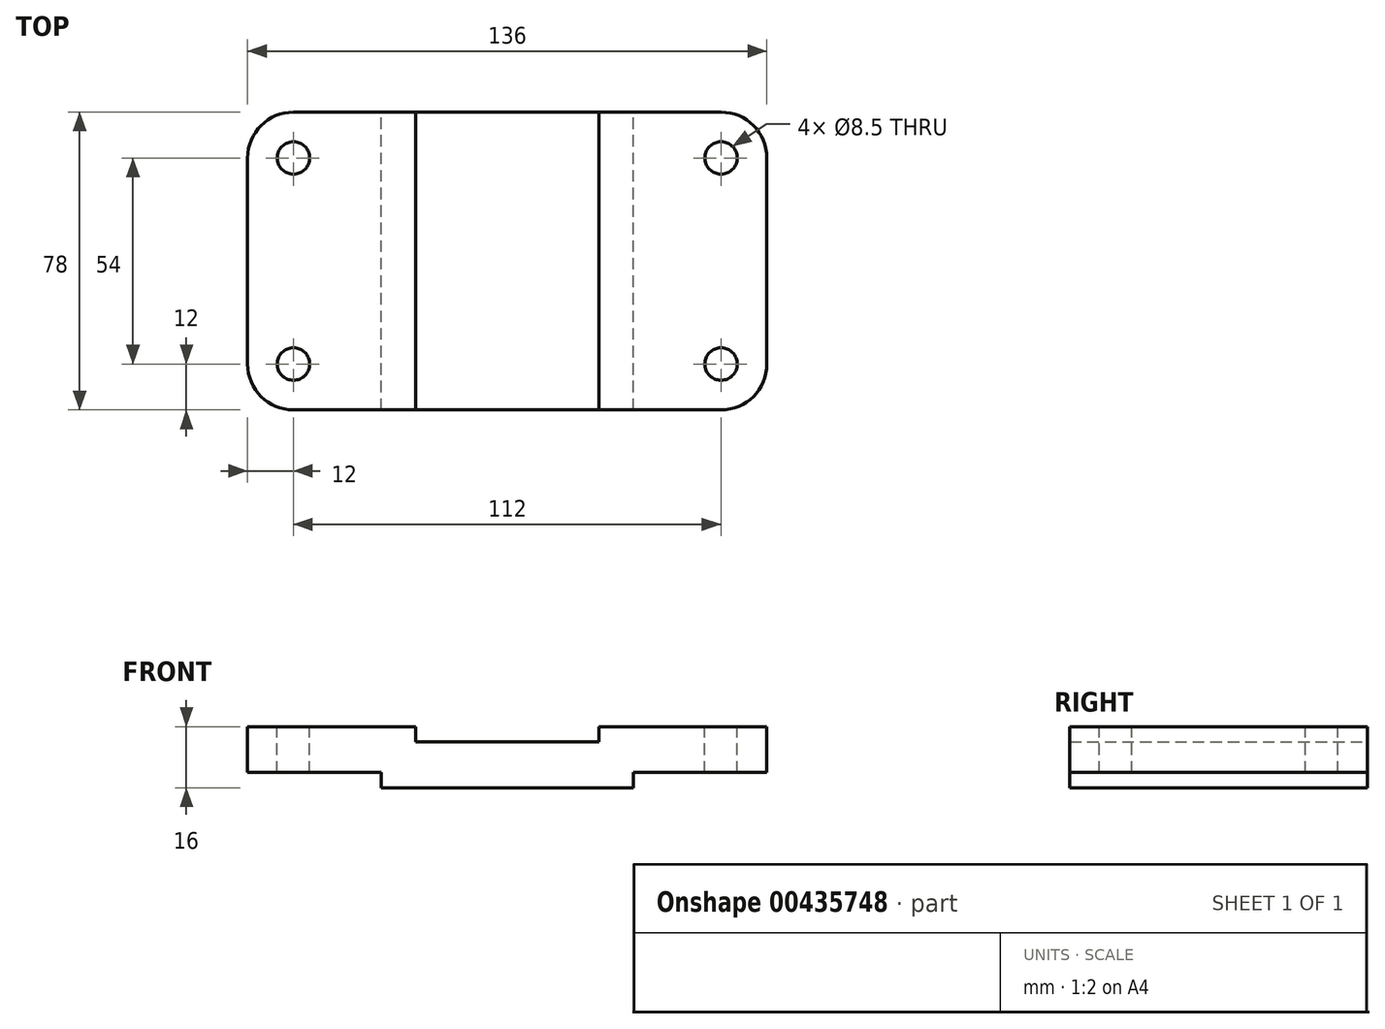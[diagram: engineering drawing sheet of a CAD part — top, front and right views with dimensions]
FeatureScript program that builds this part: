
annotation { "Feature Type Name" : "Feature", "Feature Type Description" : "" }
export const myFeature = defineFeature(function(context is Context, id is Id, definition is map)
    precondition{}
    {
        {
            var Q0;
            Q0=qCreatedBy(makeId("Front.planeOp"),FACE);
            var sketch = newSketch(context, id + "F0", { "sketchPlane" : qUnion([Q0])});
            skLineSegment(sketch, "E0.bottom", {"start": v(-33, 0) * mm, "end": v(33, 0) * mm});
            skLineSegment(sketch, "E0.top", {"start": v(-68, 16) * mm, "end": v(-24, 16) * mm});
            skLineSegment(sketch, "E0.left", {"start": v(-68, 4) * mm, "end": v(-68, 16) * mm});
            skLineSegment(sketch, "E0.right", {"start": v(68, 4) * mm, "end": v(68, 16) * mm});
            skLineSegment(sketch, "E1.top", {"start": v(-24, 12) * mm, "end": v(24, 12) * mm});
            skLineSegment(sketch, "E1.left", {"start": v(-24, 16) * mm, "end": v(-24, 12) * mm});
            skLineSegment(sketch, "E1.right", {"start": v(24, 16) * mm, "end": v(24, 12) * mm});
            skLineSegment(sketch, "E2.top", {"start": v(68, 4) * mm, "end": v(33, 4) * mm});
            skLineSegment(sketch, "E2.right", {"start": v(33, 0) * mm, "end": v(33, 4) * mm});
            skLineSegment(sketch, "E3.MirrorCS", {"start": v(-68, 4) * mm, "end": v(-33, 4) * mm});
            skLineSegment(sketch, "E4.MirrorCS", {"start": v(-33, 0) * mm, "end": v(-33, 4) * mm});
            skLineSegment(sketch, "E5.trimOffspring", {"start": v(24, 16) * mm, "end": v(68, 16) * mm});
            skPoint(sketch, "E6.orphan", {"position": v(-68, 0) * mm});
            skSolve(sketch);
        }
        {
            var Q0;
            Q0=makeQuery(id+"F0.imprint","IMPRINT",FACE,{"disambiguationData":[TD([[makeQuery(id+"F0.imprint","IMPRINT",EDGE,{"derivedFrom":sQuery(id+"F0.wireOp",EDGE,"E0.bottom")}),1.0]])]});
            extrude(context, id + "F1", {"entities" : qUnion([Q0]), "depth" : 78 * mm});
        }
        {
            var Q0;
            Q0=makeQuery(id+"F1.opExtrude","CAP_EDGE",EDGE,{"disambiguationData":[OSD([sQuery(id+"F0.wireOp",EDGE,"E0.left")])],"isStart":false});
            var Q1;
            Q1=makeQuery(id+"F1.opExtrude","CAP_EDGE",EDGE,{"disambiguationData":[OSD([sQuery(id+"F0.wireOp",EDGE,"E0.right")])],"isStart":false});
            var Q2;
            Q2=makeQuery(id+"F1.opExtrude","CAP_EDGE",EDGE,{"disambiguationData":[OSD([sQuery(id+"F0.wireOp",EDGE,"E0.right")])],"isStart":true});
            var Q3;
            Q3=makeQuery(id+"F1.opExtrude","CAP_EDGE",EDGE,{"disambiguationData":[OSD([sQuery(id+"F0.wireOp",EDGE,"E0.left")])],"isStart":true});
            fillet(context, id + "F2", {"entities" : qUnion([Q0, Q1, Q2, Q3]), "radius" : 12 * mm, "tangentPropagation" : true, "allowEdgeOverflow" : false});
        }
        {
            var Q0;
            Q0=makeQuery(id+"F1.opExtrude","SWEPT_FACE",FACE,{"disambiguationData":[OSD([sQuery(id+"F0.wireOp",EDGE,"E0.top")])]});
            var sketch = newSketch(context, id + "F3", { "sketchPlane" : qUnion([Q0])});
            skPoint(sketch, "E7", {"position": v(-56, -66) * mm});
            skPoint(sketch, "E8", {"position": v(-56, -12) * mm});
            skPoint(sketch, "E9", {"position": v(56, -12) * mm});
            skPoint(sketch, "E10", {"position": v(56, -66) * mm});
            skSolve(sketch);
        }
        {
            var Q0;
            Q0=sQuery(id+"F3.wireOp",VERTEX,"E7");
            var Q1;
            Q1=sQuery(id+"F3.wireOp",VERTEX,"E8");
            var Q2;
            Q2=sQuery(id+"F3.wireOp",VERTEX,"E10");
            var Q3;
            Q3=sQuery(id+"F3.wireOp",VERTEX,"E9");
            var Q4;
            Q4=makeQuery(id+"F1.opExtrude","SWEPT_BODY",BODY,{"disambiguationData":[OSD([sQuery(id+"F0.wireOp",EDGE,"E0.bottom"),sQuery(id+"F0.wireOp",EDGE,"E0.top"),sQuery(id+"F0.wireOp",EDGE,"E0.left"),sQuery(id+"F0.wireOp",EDGE,"E0.right"),sQuery(id+"F0.wireOp",EDGE,"E1.top"),sQuery(id+"F0.wireOp",EDGE,"E1.left"),sQuery(id+"F0.wireOp",EDGE,"E1.right"),sQuery(id+"F0.wireOp",EDGE,"E2.top"),sQuery(id+"F0.wireOp",EDGE,"E2.right"),sQuery(id+"F0.wireOp",EDGE,"E3.MirrorCS"),sQuery(id+"F0.wireOp",EDGE,"E4.MirrorCS"),sQuery(id+"F0.wireOp",EDGE,"E5.trimOffspring")])]});
            hole(context, id + "F4", {"style" : HoleStyle.SIMPLE, "endStyle" : HoleEndStyle.THROUGH, "standardTappedOrClearance" : lookupTablePath({ "standard" : "ISO", "engagement" : "75%", "pitch" : "1.5 mm", "size" : "M10", "type" : "Tapped" }), "standardBlindInLast" : lookupTablePath({ "standard" : "ISO", "engagement" : "75%", "pitch" : "1.5 mm", "size" : "M10", "type" : "Tapped" }), "holeDiameter" : 8.5 * mm, "showTappedDepth" : true, "isTappedThrough" : true, "tappedDepth" : 7.24 * mm, "tapClearance" : 3, "startFromSketch" : true, "locations" : qUnion([Q0, Q1, Q2, Q3]), "scope" : qUnion([Q4]), "majorDiameter" : 10 * mm});
        }
    });
